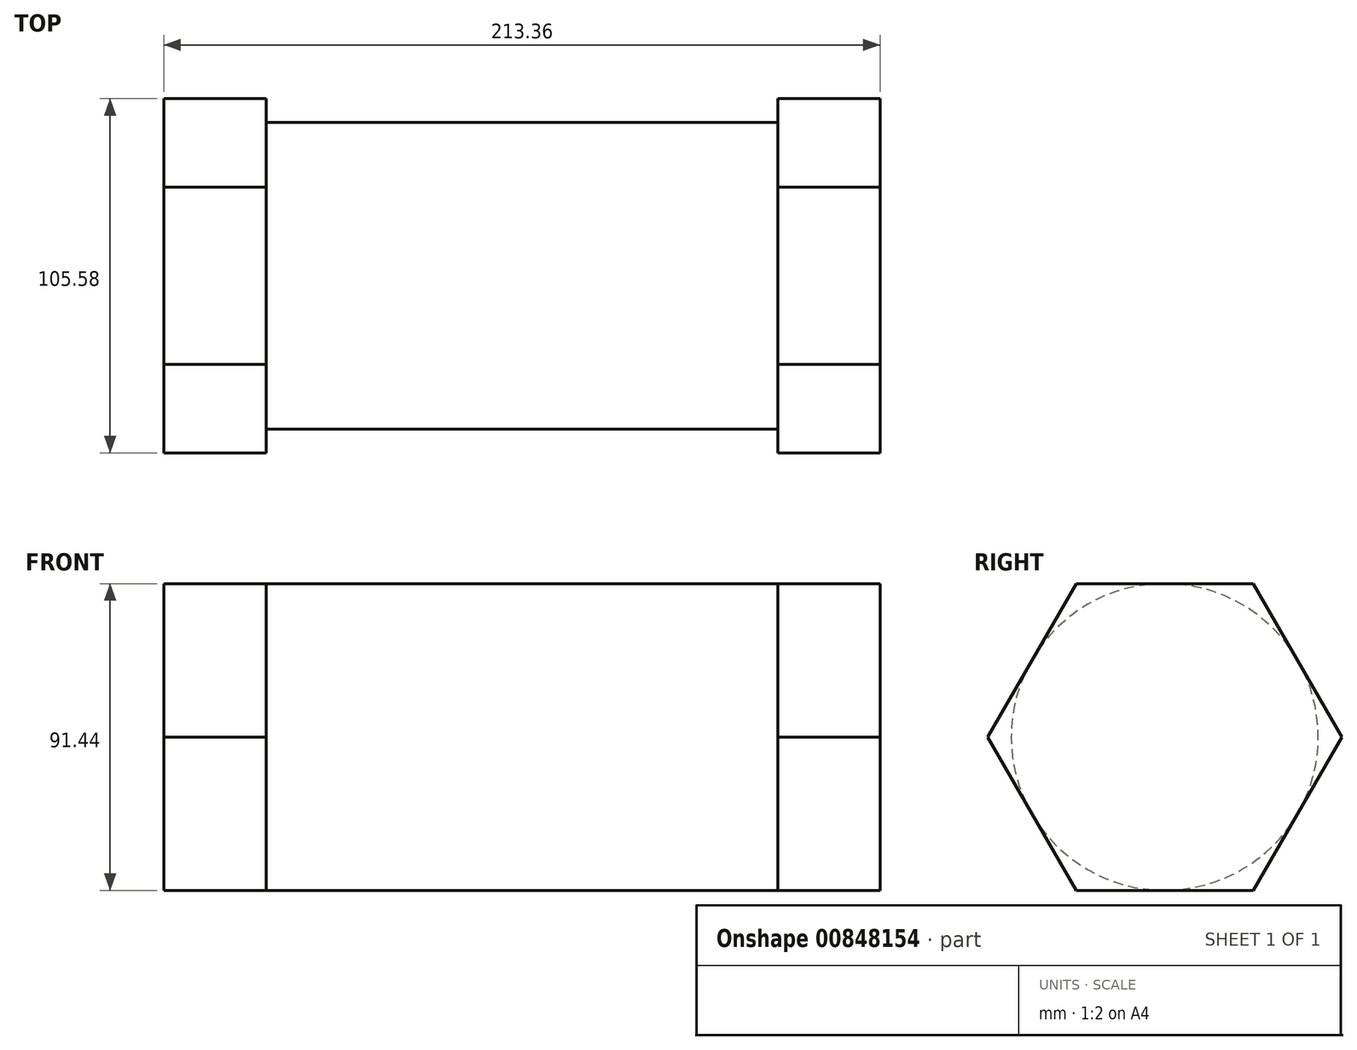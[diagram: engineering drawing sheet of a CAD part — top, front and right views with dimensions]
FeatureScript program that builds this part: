
annotation { "Feature Type Name" : "Feature", "Feature Type Description" : "" }
export const myFeature = defineFeature(function(context is Context, id is Id, definition is map)
    precondition{}
    {
        {
            var Q0;
            Q0=qCreatedBy(makeId("Right.planeOp"),FACE);
            var sketch = newSketch(context, id + "F0", { "sketchPlane" : qUnion([Q0])});
            skCircle(sketch, "E0", {"center": v(0, 0) * mm, "radius": 45.72 * mm});
            skSolve(sketch);
        }
        {
            var Q0;
            Q0 = qSketchRegion(id + "F0", true);
            extrude(context, id + "F1", {"entities" : qUnion([Q0]), "depth" : 76.2 * mm, "offsetDistance" : 30.48 * mm});
        }
        {
            var Q0;
            Q0=makeQuery(id+"F1.opExtrude","CAP_FACE",FACE,{"disambiguationData":[OSD([sQuery(id+"F0.wireOp",EDGE,"E0")])],"isStart":false});
            var sketch = newSketch(context, id + "F2", { "sketchPlane" : qUnion([Q0])});
            skCircle(sketch, "E1.cCircle", {"center": v(0, 0) * mm, "radius": 45.72 * mm, "construction": true});
            skLineSegment(sketch, "E1.0", {"start": v(26.4, -45.72) * mm, "end": v(-26.4, -45.72) * mm});
            skLineSegment(sketch, "E1.1", {"start": v(-26.4, -45.72) * mm, "end": v(-52.8, 0) * mm});
            skLineSegment(sketch, "E1.2", {"start": v(-52.8, 0) * mm, "end": v(-26.4, 45.72) * mm});
            skLineSegment(sketch, "E1.3", {"start": v(-26.4, 45.72) * mm, "end": v(26.4, 45.72) * mm});
            skLineSegment(sketch, "E1.4", {"start": v(26.4, 45.72) * mm, "end": v(52.8, 0) * mm});
            skLineSegment(sketch, "E1.5", {"start": v(52.8, 0) * mm, "end": v(26.4, -45.72) * mm});
            skPoint(sketch, "E1.0.midPoint", {"position": v(0, -45.72) * mm});
            skSolve(sketch);
        }
        {
            var Q0;
            Q0 = qSketchRegion(id + "F2", true);
            extrude(context, id + "F3", {"entities" : qUnion([Q0]), "operationType" : NewBodyOperationType.ADD, "depth" : 30.48 * mm, "offsetDistance" : 30.48 * mm});
        }
        {
            var Q0;
            Q0=makeQuery(id+"F1.opExtrude","SWEPT_BODY",BODY,{"disambiguationData":[OSD([sQuery(id+"F0.wireOp",EDGE,"E0")])]});
            var Q1;
            Q1=qCreatedBy(makeId("Right.planeOp"),FACE);
            mirror(context, id + "F4", {"operationType" : NewBodyOperationType.ADD, "entities" : qUnion([Q0]), "mirrorPlane" : qUnion([Q1])});
        }
    });
